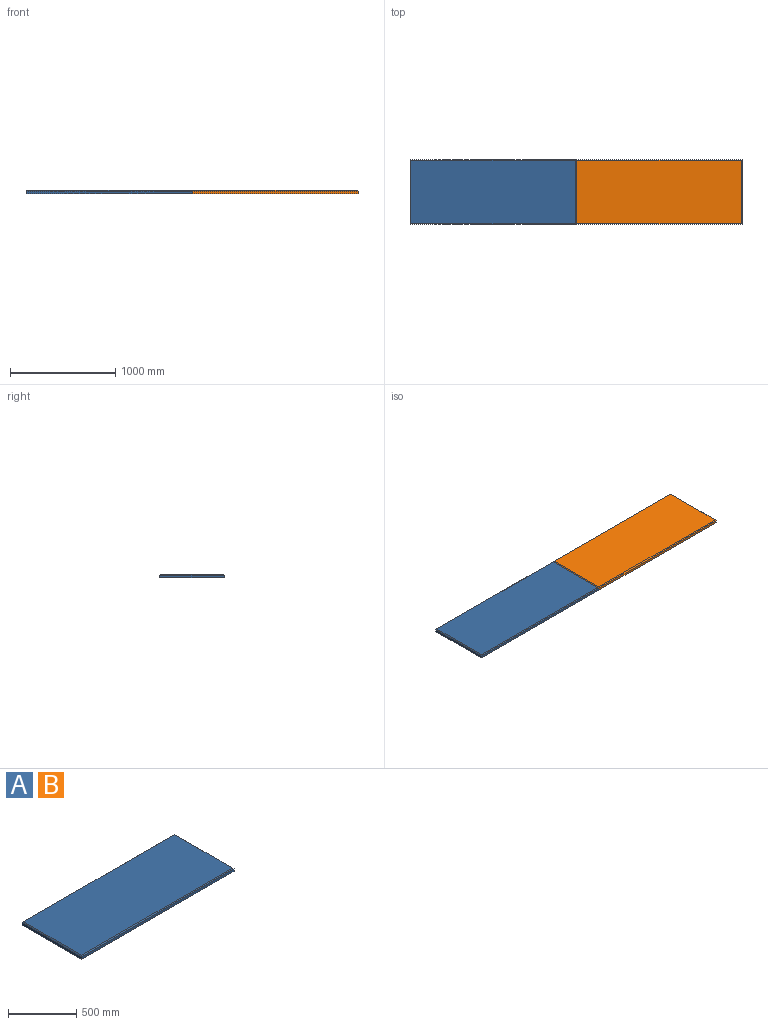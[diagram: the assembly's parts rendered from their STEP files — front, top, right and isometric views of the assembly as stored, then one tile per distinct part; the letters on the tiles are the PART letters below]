
ASSEMBLY  parts=2 mates=1
PART A: 10 faces, bbox 1575x615x30 mm
  f0: plane 1575x615mm, normal (0,0,-1), area 968625mm2, adj f1,f2,f3,f4
  f1: plane 1575x22mm, normal (0,-1,0), area 34650mm2, adj f0,f2,f4,f7
  f2: plane 615x22mm, normal (1,0,0), area 13530mm2, adj f0,f1,f3,f9
  f3: plane 1575x22mm, normal (0,1,0), area 34650mm2, adj f0,f2,f4,f8
  f4: plane 615x22mm, normal (-1,0,0), area 13530mm2, adj f0,f1,f3,f6
  f5: plane 1559x599mm, normal (0,0,1), area 933841mm2, adj f6,f7,f8,f9
  f6: plane 615x8mm, normal (-0.71,0,0.71), area 6867.4mm2, adj f4,f5,f7,f8
  f7: plane 1575x8mm, normal (0,-0.71,0.71), area 17728.6mm2, adj f1,f5,f6,f9
  f8: plane 1575x8mm, normal (0,0.71,0.71), area 17728.6mm2, adj f3,f5,f6,f9
  f9: plane 615x8mm, normal (0.71,0,0.71), area 6867.4mm2, adj f2,f5,f7,f8
PART B: same geometry as A
PLACE A t=(1575,1500,1530)mm
PLACE B t=(3150,1500,1530)mm
MATE fastened B.f0 <-> A.f0  axis (0,0,-1) through (1575,0,0)mm
